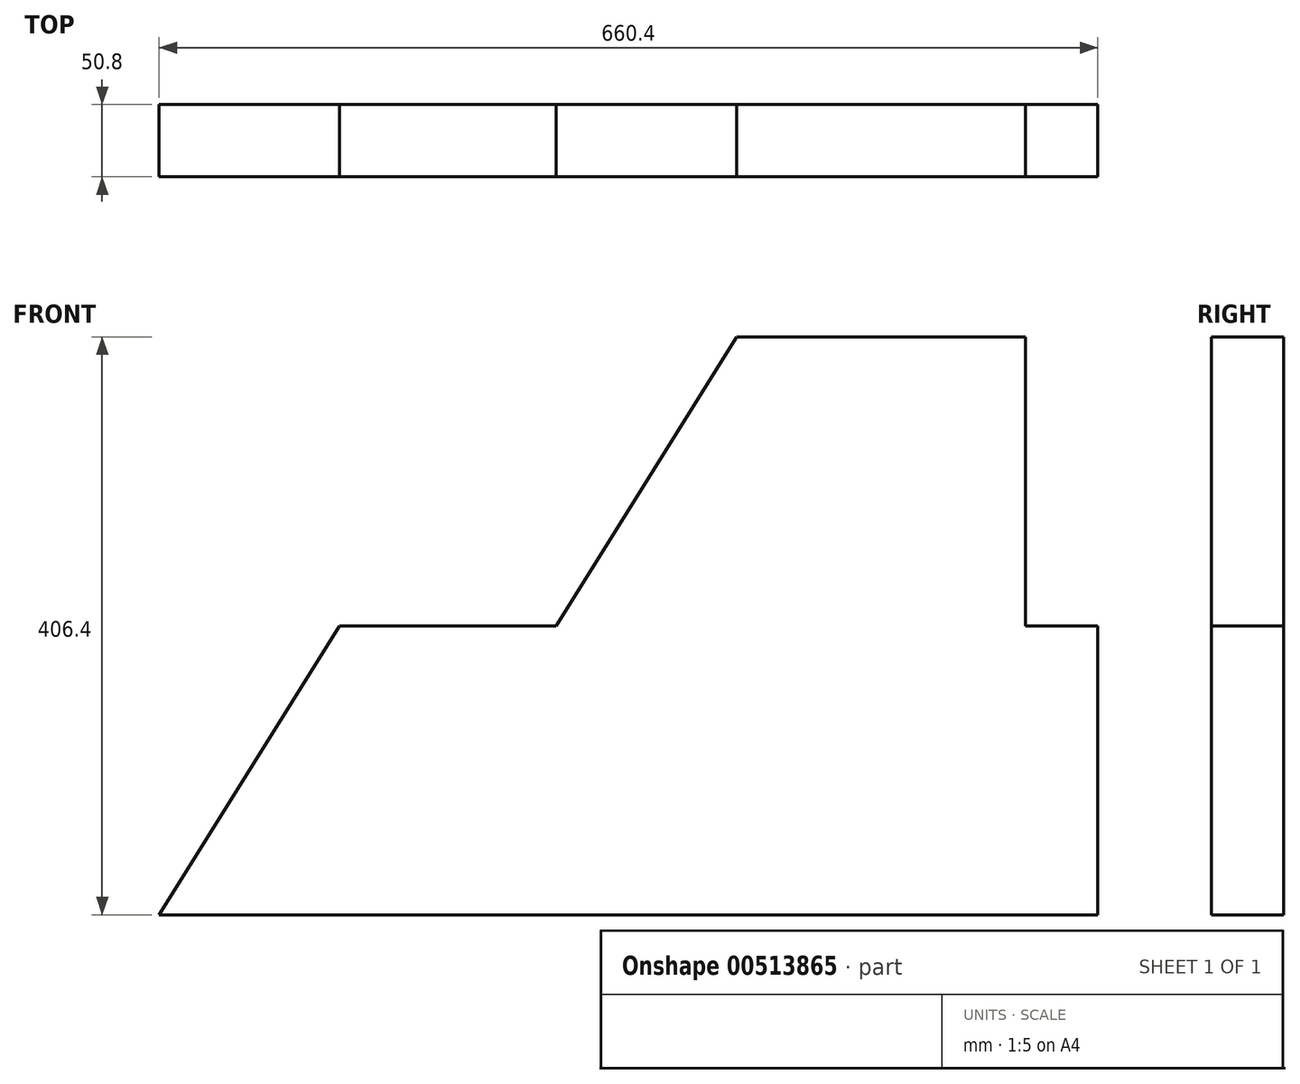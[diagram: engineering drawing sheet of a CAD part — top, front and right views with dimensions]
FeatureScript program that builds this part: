
annotation { "Feature Type Name" : "Feature", "Feature Type Description" : "" }
export const myFeature = defineFeature(function(context is Context, id is Id, definition is map)
    precondition{}
    {
        {
            var Q0;
            Q0=qCreatedBy(makeId("Front.planeOp"),FACE);
            var sketch = newSketch(context, id + "F0", { "sketchPlane" : qUnion([Q0])});
            skLineSegment(sketch, "E0", {"start": v(-57.42, -31.3) * mm, "end": v(602.98, -31.3) * mm});
            skLineSegment(sketch, "E1", {"start": v(602.98, -31.3) * mm, "end": v(602.98, 171.9) * mm});
            skLineSegment(sketch, "E2", {"start": v(602.98, 171.9) * mm, "end": v(552.18, 171.9) * mm});
            skLineSegment(sketch, "E3", {"start": v(552.18, 171.9) * mm, "end": v(552.18, 375.1) * mm});
            skLineSegment(sketch, "E4", {"start": v(552.18, 375.1) * mm, "end": v(348.98, 375.1) * mm});
            skLineSegment(sketch, "E5", {"start": v(348.98, 375.1) * mm, "end": v(221.98, 171.9) * mm});
            skLineSegment(sketch, "E6", {"start": v(221.98, 171.9) * mm, "end": v(69.58, 171.9) * mm});
            skLineSegment(sketch, "E7", {"start": v(69.58, 171.9) * mm, "end": v(-57.42, -31.3) * mm});
            skSolve(sketch);
        }
        {
            var Q0;
            Q0=makeQuery(id+"F0.imprint","IMPRINT",FACE,{"disambiguationData":[TD([[makeQuery(id+"F0.imprint","IMPRINT",EDGE,{"derivedFrom":sQuery(id+"F0.wireOp",EDGE,"E0")}),1.0]])]});
            extrude(context, id + "F1", {"entities" : qUnion([Q0]), "depth" : 50.8 * mm, "offsetDistance" : 25.4 * mm});
        }
    });
